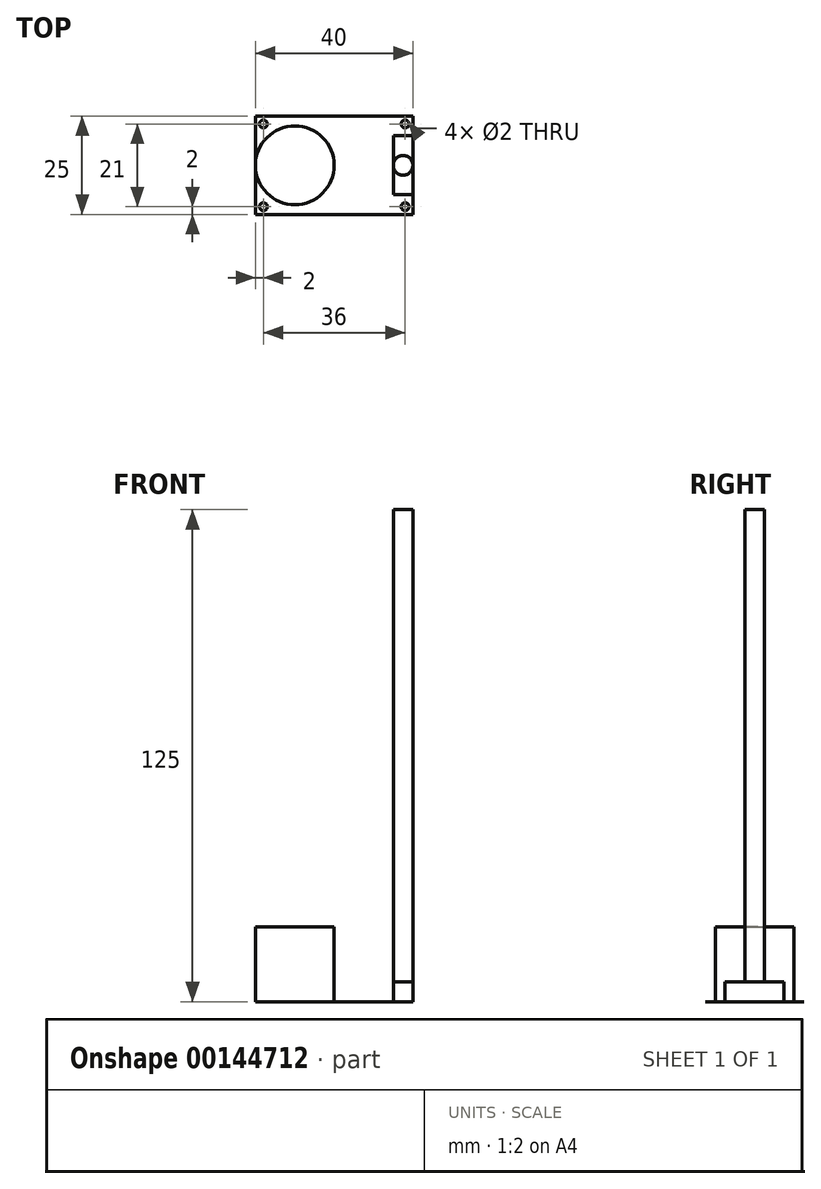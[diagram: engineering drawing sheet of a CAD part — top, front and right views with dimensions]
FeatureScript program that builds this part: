
annotation { "Feature Type Name" : "Feature", "Feature Type Description" : "" }
export const myFeature = defineFeature(function(context is Context, id is Id, definition is map)
    precondition{}
    {
        {
            var Q0;
            Q0=qCreatedBy(makeId("Top.planeOp"),FACE);
            var sketch = newSketch(context, id + "F0", { "sketchPlane" : qUnion([Q0])});
            skLineSegment(sketch, "E0.bottom", {"start": v(20, 12.5) * mm, "end": v(-20, 12.5) * mm});
            skLineSegment(sketch, "E0.top", {"start": v(20, -12.5) * mm, "end": v(-20, -12.5) * mm});
            skLineSegment(sketch, "E0.left", {"start": v(20, 12.5) * mm, "end": v(20, -12.5) * mm});
            skLineSegment(sketch, "E0.right", {"start": v(-20, 12.5) * mm, "end": v(-20, -12.5) * mm});
            skPoint(sketch, "E0.middle", {"position": v(0, 0) * mm});
            skLineSegment(sketch, "E1.bottom", {"start": v(18, 10.5) * mm, "end": v(-18, 10.5) * mm, "construction": true});
            skLineSegment(sketch, "E1.top", {"start": v(18, -10.5) * mm, "end": v(-18, -10.5) * mm, "construction": true});
            skLineSegment(sketch, "E1.left", {"start": v(18, 10.5) * mm, "end": v(18, -10.5) * mm, "construction": true});
            skLineSegment(sketch, "E1.right", {"start": v(-18, 10.5) * mm, "end": v(-18, -10.5) * mm, "construction": true});
            skCircle(sketch, "E2", {"center": v(-18, 10.5) * mm, "radius": 1 * mm});
            skCircle(sketch, "E3", {"center": v(-18, -10.5) * mm, "radius": 1 * mm});
            skCircle(sketch, "E4", {"center": v(18, -10.5) * mm, "radius": 1 * mm});
            skCircle(sketch, "E5", {"center": v(18, 10.5) * mm, "radius": 1 * mm});
            skSolve(sketch);
        }
        {
            var Q0;
            Q0=makeQuery(id+"F0.imprint","IMPRINT",FACE,{"disambiguationData":[TD([[makeQuery(id+"F0.imprint","IMPRINT",EDGE,{"derivedFrom":sQuery(id+"F0.wireOp",EDGE,"E0.bottom")}),1.0]])]});
            extrude(context, id + "F1", {"entities" : qUnion([Q0]), "depth" : 1 / 406.4 * mm});
        }
        {
            var Q0;
            Q0=makeQuery(id+"F1.opExtrude","CAP_FACE",FACE,{"disambiguationData":[OSD([sQuery(id+"F0.wireOp",EDGE,"E0.bottom"),sQuery(id+"F0.wireOp",EDGE,"E0.top"),sQuery(id+"F0.wireOp",EDGE,"E0.left"),sQuery(id+"F0.wireOp",EDGE,"E0.right"),sQuery(id+"F0.wireOp",EDGE,"E2"),sQuery(id+"F0.wireOp",EDGE,"E3"),sQuery(id+"F0.wireOp",EDGE,"E4"),sQuery(id+"F0.wireOp",EDGE,"E5")])],"isStart":false});
            var sketch = newSketch(context, id + "F2", { "sketchPlane" : qUnion([Q0])});
            skCircle(sketch, "E6", {"center": v(-10, 0) * mm, "radius": 10 * mm});
            skPoint(sketch, "E6.centerSnap0", {"position": v(-20, 0) * mm});
            skSolve(sketch);
        }
        {
            var Q0;
            Q0 = qSketchRegion(id + "F2", true);
            extrude(context, id + "F3", {"entities" : qUnion([Q0]), "depth" : 19 * mm});
        }
        {
            var Q0;
            Q0=makeQuery(id+"F1.opExtrude","CAP_FACE",FACE,{"disambiguationData":[OSD([sQuery(id+"F0.wireOp",EDGE,"E0.bottom"),sQuery(id+"F0.wireOp",EDGE,"E0.top"),sQuery(id+"F0.wireOp",EDGE,"E0.left"),sQuery(id+"F0.wireOp",EDGE,"E0.right"),sQuery(id+"F0.wireOp",EDGE,"E2"),sQuery(id+"F0.wireOp",EDGE,"E3"),sQuery(id+"F0.wireOp",EDGE,"E4"),sQuery(id+"F0.wireOp",EDGE,"E5")])],"isStart":false});
            var sketch = newSketch(context, id + "F4", { "sketchPlane" : qUnion([Q0])});
            skLineSegment(sketch, "E7.bottom", {"start": v(15, 7.5) * mm, "end": v(20, 7.5) * mm});
            skLineSegment(sketch, "E7.top", {"start": v(15, -7.5) * mm, "end": v(20, -7.5) * mm});
            skLineSegment(sketch, "E7.left", {"start": v(15, 7.5) * mm, "end": v(15, -7.5) * mm});
            skLineSegment(sketch, "E7.right", {"start": v(20, 7.5) * mm, "end": v(20, -7.5) * mm});
            skPoint(sketch, "E8", {"position": v(15, 0) * mm});
            skSolve(sketch);
        }
        {
            var Q0;
            Q0 = qSketchRegion(id + "F4", true);
            extrude(context, id + "F5", {"entities" : qUnion([Q0]), "depth" : 5 * mm});
        }
        {
            var Q0;
            Q0=makeQuery(id+"F5.opExtrude","CAP_FACE",FACE,{"disambiguationData":[OSD([sQuery(id+"F4.wireOp",EDGE,"E7.bottom"),sQuery(id+"F4.wireOp",EDGE,"E7.top"),sQuery(id+"F4.wireOp",EDGE,"E7.left"),sQuery(id+"F4.wireOp",EDGE,"E7.right")])],"isStart":false});
            var sketch = newSketch(context, id + "F6", { "sketchPlane" : qUnion([Q0])});
            skCircle(sketch, "E9", {"center": v(17.5, 0) * mm, "radius": 2.5 * mm});
            skSolve(sketch);
        }
        {
            var Q0;
            Q0 = qSketchRegion(id + "F6", true);
            extrude(context, id + "F7", {"entities" : qUnion([Q0]), "operationType" : NewBodyOperationType.ADD, "depth" : 120 * mm});
        }
    });
